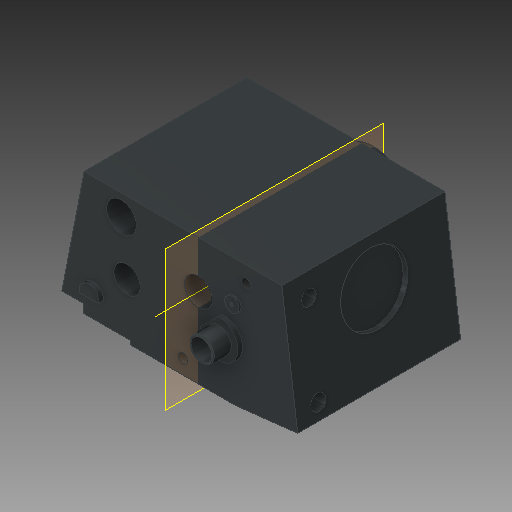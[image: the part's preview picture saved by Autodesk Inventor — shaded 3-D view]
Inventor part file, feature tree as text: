
AUTODESK INVENTOR PART (.ipt)
format: ipt  version: 2018 (Build 220112000, 112)  size: 356,352 bytes
history: native  units: in
note: dims shown in document units (in); Inventor stores cm internally (conversion verified against a paired STEP export)
features: sketch x18, extrude x17, fillet x2, thread x2, chamfer x1, hole x1, plane x1, other x1
ambient origin geometry x8: Origin, YZ Plane, XZ Plane, XY Plane, X Axis, Y Axis, Z Axis, Center Point
bodies: Solid1 (feature_tree)
feature tree (43):
  extrude  "Extrusion1"  Depth=10.4921in
  sketch  "Sketch3"  dims[d7=10.0in d8=0.5669in]
  extrude  "Extrusion2"  Depth=0.5669in
  extrude  "Extrusion3"  Depth=0.694in
  extrude  "Extrusion4"  Depth=0.7087in
  extrude  "Extrusion5"  Depth=0.0787in
  extrude  "Extrusion6"  Depth=13.4646in TaperAngle=0.0deg
  fillet  "Fillet1"  Radius=5.5118in
  fillet  "Fillet2"  Radius=6.2992in
  extrude  "Extrusion7"  Depth=2.7559in
  thread  "Thread1"  [1 undecoded]
  extrude  "Extrusion8"  Depth=1.1811in
  extrude  "Extrusion9"  Depth=1.7717in
  extrude  "Extrusion10"  Depth=1.2106in
  chamfer  "Chamfer1"  Distance=2.3622in
  extrude  "Extrusion11"  Depth=0.748in
  extrude  "Extrusion12"  Depth=1.0236in TaperAngle=0.0deg
  extrude  "Extrusion13"  Depth=1.0236in TaperAngle=0.0deg
  extrude  "Extrusion14"  Depth=1.378in
  hole  "Hole1"  [1 undecoded]
  extrude  "Extrusion15"  Depth=0.0787in
  extrude  "Extrusion16"  Depth=0.7874in
  extrude  "Extrusion17"  Depth=1.1811in TaperAngle=0.0deg
  thread  "Thread2"  [1 undecoded]
  plane  "Work Plane2"
  sketch  "Sketch1"  dims[d0=8.6614in d1=10.4921in]
  sketch  "Sketch4"  dims[d9=9.6457in d10=0.694in]
  sketch  "Sketch5"  dims[d11=1.7717in d12=0.7087in]
  sketch  "Sketch6"  dims[d14=16.3386in d15=0.0787in]
  sketch  "Sketch7"  dims[d16=0.0787in d17=13.4646in d18=0.0in d22=5.5118in d26=6.2992in]
  sketch  "Sketch8"  dims[d27=2.7559in d28=3.6024in d29=2.7559in]
  sketch  "Sketch10"  dims[d30=0.3937in d31=0.0in d34=1.1811in]
  sketch  "Sketch11"  dims[d37=1.7717in d38=2.0079in]
  sketch  "Sketch12"  dims[d39=1.2402in d42=1.2106in]
  sketch  "Sketch13"  dims[d43=1.8799in d44=2.3622in d45=0.0in]
  sketch  "Sketch14"  dims[d49=6.3386in d50=0.748in]
  sketch  "Sketch15"  dims[d52=7.4213in d53=1.0236in d54=0.0in]
  sketch  "Sketch16"  dims[d55=2.2835in d56=1.0236in d57=0.0in]
  sketch  "Sketch17"  dims[d69=0.7874in d70=1.378in]
  sketch  "Sketch19"  dims[d72=0.3937in d73=0.315in]
  sketch  "Sketch20"  dims[d75=0.2362in d76=0.0in d77=0.0787in]
  sketch  "Sketch21"  dims[d78=0.0787in d82=0.7874in d83=1.1811in d84=0.0in d85=0.3937in d86=0.0in d87=3.0118in d88=45.0deg d91=0.3937in d92=0.0in d93=2.0079in d94=1.6929in d95=1.4961in d96=0.0in d97=1.9685in d98=0.0in d99=0.0787in d100=0.0787in d101=45.0deg d103=1.1811in d105=0.3937in d106=0.0in d107=5.9055in d108=5.9646in d109=90.0deg d110=2.7559in d111=7.4803in d112=90.0deg d113=0.3937in d114=0.0in d116=0.3937in d117=0.0in d118=2.9528in d120=3.2283in d121=1.1811in d122=0.1969in d123=0.0in d124=0.2559in d125=0.1181in d126=0.2362in d127=0.2559in d128=0.0787in d129=90.0deg d130=0.1969in d131=0.0in d132=6.6929in d133=90.0deg d134=1.7323in d135=2.4409in d136=0.7874in d137=0.0in d138=5.9055in d139=5.9646in d140=90.0deg d141=2.1654in d142=2.7559in d143=0.0in d144=0.9843in d145=1.3386in d146=0.7874in d147=0.7874in d148=0.0in d149=0.3937in d150=0.0in d151=0.0in]
  other  "Work Axis1"
note: 3 required parameter values undecoded (feature->parameter linkage not recoverable at this tier; creation-order binding heuristic only, values carry confidence <= 0.55)
